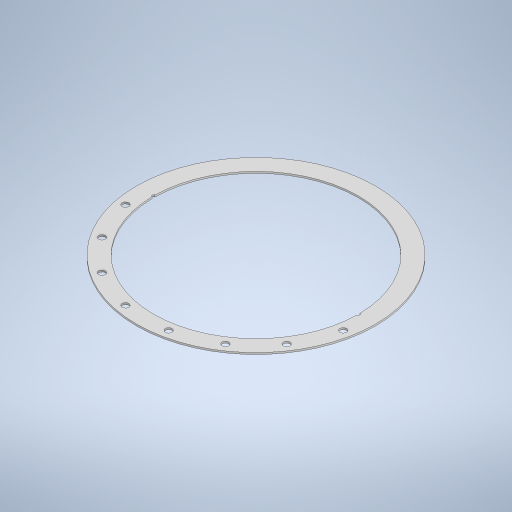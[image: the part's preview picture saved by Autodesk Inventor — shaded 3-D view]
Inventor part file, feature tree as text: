
AUTODESK INVENTOR PART (.ipt)
format: ipt  version: 2024.2 (Build 282272000, 272)  size: 321,536 bytes
history: native  units: mm
features: sketch x3, extrude x2, other x2, sheet_metal_op x1, pattern_circular x1, projected_geometry x1
ambient origin geometry x8: Origin, YZ Plane, XZ Plane, XY Plane, X Axis, Y Axis, Z Axis, Center Point
bodies: Solid1 (feature_tree)
feature tree (10):
  sheet_metal_op  "Face1"
  extrude  "Extrusion1"  TaperAngle=0.0deg  [1 undecoded]
  pattern_circular  "Circular Pattern1"  Count=8 Angle=157.5deg
  extrude  "Extrusion2"  Depth=30.0mm
  sketch  "Sketch1"  dims[d2=3.0mm d4=0.0mm d5=0.0mm d6=80.0mm d7=157.5deg]
  other  "Plate1"
  sketch  "Sketch2"  dims[d9=390.0mm d11=30.0mm]
  projected_geometry  "Projected Loop1"
  sketch  "Sketch3"  dims[d20=1.963495mm d21=12.0mm d25=0.0mm d26=0.0mm d27=5.0mm d29=80.0mm d30=0.5mm d31=0.872665mm d32=0.5mm d33=0.872665mm]
  other  "Definition1"
note: 1 required parameter value undecoded (feature->parameter linkage not recoverable at this tier; creation-order binding heuristic only, values carry confidence <= 0.55)
